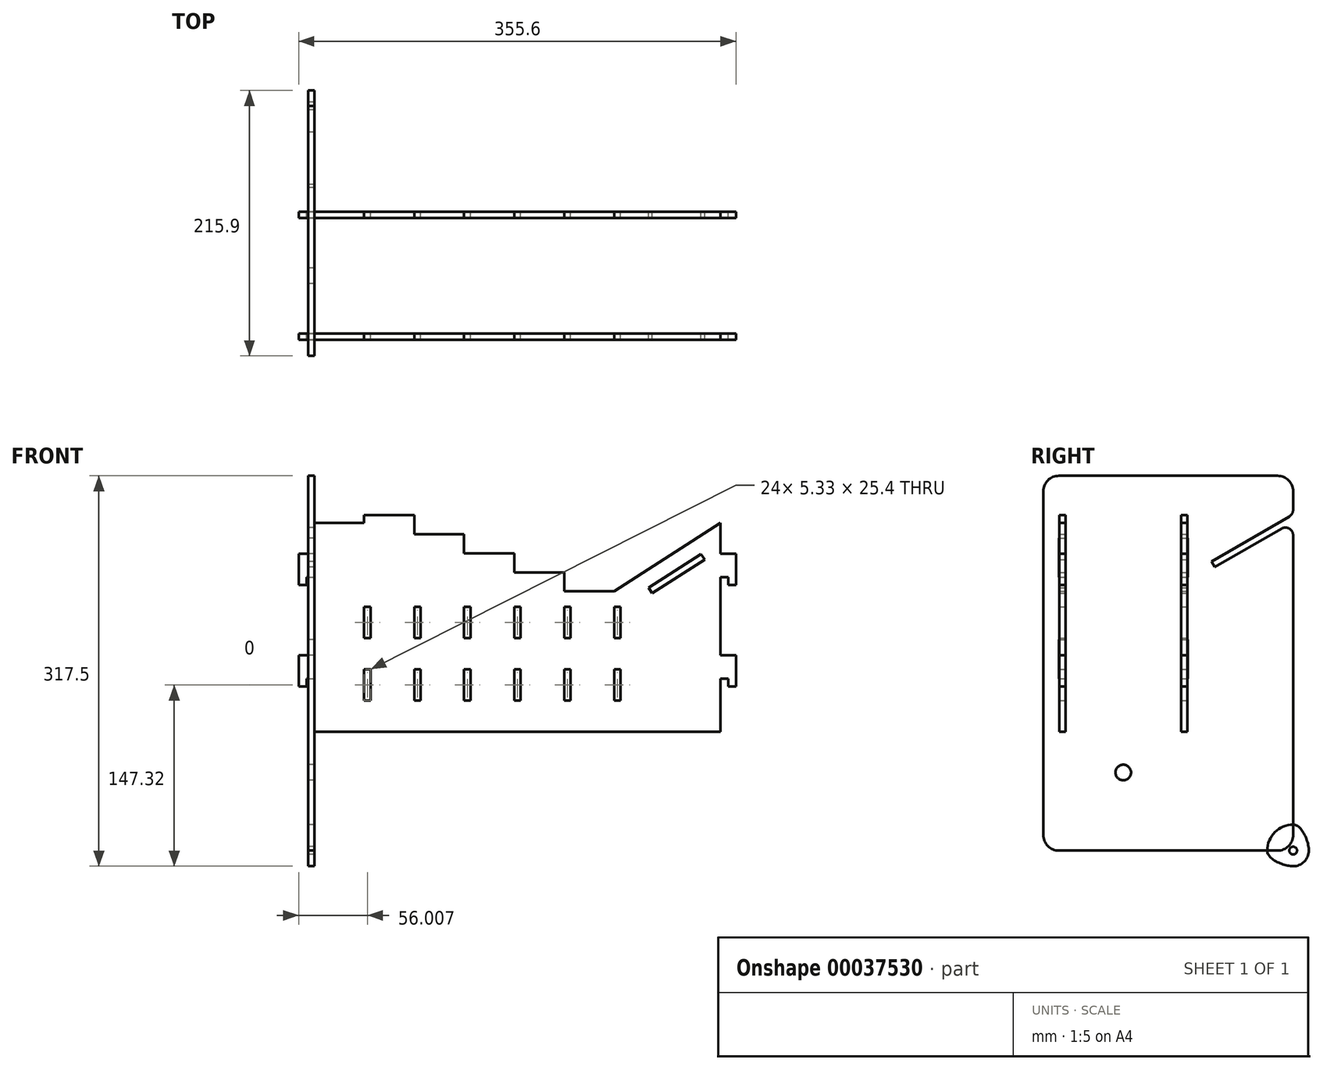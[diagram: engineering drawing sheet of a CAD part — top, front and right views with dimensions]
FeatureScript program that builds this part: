
annotation { "Feature Type Name" : "Feature", "Feature Type Description" : "" }
export const myFeature = defineFeature(function(context is Context, id is Id, definition is map)
    precondition{}
    {
        {
            var Q0;
            Q0=qCreatedBy(makeId("Right.planeOp"),FACE);
            var sketch = newSketch(context, id + "F0", { "sketchPlane" : qUnion([Q0])});
            skCircle(sketch, "E0", {"center": v(0, 0) * mm, "radius": 12.7 * mm});
            skArc(sketch, "E1", {"start": v(0, 21.08) * mm, "mid": v(-14.9, 14.9) * mm, "end": v(-21.08, 0) * mm});
            skLineSegment(sketch, "E2", {"start": v(0, 32.39) * mm, "end": v(0, -38.1) * mm, "construction": true});
            skLineSegment(sketch, "E3", {"start": v(-51.8, 0) * mm, "end": v(46.08, 0) * mm, "construction": true});
            skFitSpline(sketch, "E4", {"points": [v(0, 21.08) * mm, v(12.7, 0) * mm], "startDerivative": vector(20.97, 0) * mm, "endDerivative": vector(0, -23.76) * mm});
            skLineSegment(sketch, "E5", {"start": v(0, 0) * mm, "end": v(-27.33, 27.33) * mm, "construction": true});
            skFitSpline(sketch, "E6.MirrorCS", {"points": [v(-21.08, 0) * mm, v(0, -12.7) * mm], "startDerivative": vector(0, -20.97) * mm, "endDerivative": vector(23.76, 0) * mm});
            skCircle(sketch, "E7", {"center": v(0, 0) * mm, "radius": 3.18 * mm});
            skSolve(sketch);
        }
        {
            var Q0;
            Q0 = qSketchRegion(id + "F0", true);
            extrude(context, id + "F1", {"entities" : qUnion([Q0]), "depth" : 5.08 * mm});
        }
        {
            var Q0;
            Q0=qCreatedBy(makeId("Right.planeOp"),FACE);
            var sketch = newSketch(context, id + "F2", { "sketchPlane" : qUnion([Q0])});
            skLineSegment(sketch, "E8.bottom", {"start": v(-12.7, 0) * mm, "end": v(-190.5, 0) * mm});
            skLineSegment(sketch, "E8.top", {"start": v(-12.7, 304.8) * mm, "end": v(-190.5, 304.8) * mm});
            skLineSegment(sketch, "E8.left", {"start": v(0, 12.7) * mm, "end": v(0, 256.39) * mm});
            skLineSegment(sketch, "E8.right", {"start": v(-203.2, 12.7) * mm, "end": v(-203.2, 292.1) * mm});
            skLineSegment(sketch, "E9.bottom", {"start": v(-190.5, 254) * mm, "end": v(-185.17, 254) * mm});
            skLineSegment(sketch, "E9.top", {"start": v(-190.5, 139.7) * mm, "end": v(-185.17, 139.7) * mm});
            skLineSegment(sketch, "E9.left", {"start": v(-190.5, 254) * mm, "end": v(-190.5, 222.25) * mm});
            skLineSegment(sketch, "E9.right", {"start": v(-185.17, 254) * mm, "end": v(-185.17, 222.25) * mm});
            skLineSegment(sketch, "E10.bottom", {"start": v(-91.19, 254) * mm, "end": v(-85.85, 254) * mm});
            skLineSegment(sketch, "E10.top", {"start": v(-91.19, 139.7) * mm, "end": v(-85.85, 139.7) * mm});
            skLineSegment(sketch, "E10.left", {"start": v(-91.19, 254) * mm, "end": v(-91.19, 222.25) * mm});
            skLineSegment(sketch, "E10.right", {"start": v(-85.85, 254) * mm, "end": v(-85.85, 222.25) * mm});
            skLineSegment(sketch, "E11", {"start": v(-190.5, 222.25) * mm, "end": v(-185.17, 222.25) * mm});
            skLineSegment(sketch, "E12", {"start": v(-190.5, 171.45) * mm, "end": v(-185.17, 171.45) * mm});
            skLineSegment(sketch, "E13.trimOffspring", {"start": v(-91.19, 171.45) * mm, "end": v(-85.85, 171.45) * mm});
            skLineSegment(sketch, "E14.trimOffspring", {"start": v(-91.19, 222.25) * mm, "end": v(-85.85, 222.25) * mm});
            skLineSegment(sketch, "E15.trimOffspring", {"start": v(-185.17, 171.45) * mm, "end": v(-185.17, 139.7) * mm});
            skLineSegment(sketch, "E16.trimOffspring", {"start": v(-190.5, 171.45) * mm, "end": v(-190.5, 139.7) * mm});
            skLineSegment(sketch, "E17.trimOffspring", {"start": v(-85.85, 171.45) * mm, "end": v(-85.85, 139.7) * mm});
            skLineSegment(sketch, "E18.trimOffspring", {"start": v(-91.19, 171.45) * mm, "end": v(-91.19, 139.7) * mm});
            skLineSegment(sketch, "E19", {"start": v(-3.17, 271.71) * mm, "end": v(-66.37, 235.23) * mm});
            skLineSegment(sketch, "E20", {"start": v(-66.37, 235.23) * mm, "end": v(-63.7, 230.6) * mm});
            skLineSegment(sketch, "E21", {"start": v(-63.7, 230.6) * mm, "end": v(-9.53, 261.89) * mm});
            skLineSegment(sketch, "E22.trimOffspring", {"start": v(0, 277.21) * mm, "end": v(0, 292.1) * mm});
            skPoint(sketch, "E23.visualSharp", {"position": v(0, 304.8) * mm});
            skArc(sketch, "E23.filletArc", {"start": v(0, 292.1) * mm, "mid": v(-3.72, 301.08) * mm, "end": v(-12.7, 304.8) * mm});
            skPoint(sketch, "E24.visualSharp", {"position": v(-203.2, 304.8) * mm});
            skArc(sketch, "E24.filletArc", {"start": v(-190.5, 304.8) * mm, "mid": v(-199.48, 301.08) * mm, "end": v(-203.2, 292.1) * mm});
            skPoint(sketch, "E25.visualSharp", {"position": v(-203.2, 0) * mm});
            skArc(sketch, "E25.filletArc", {"start": v(-203.2, 12.7) * mm, "mid": v(-199.48, 3.72) * mm, "end": v(-190.5, 0) * mm});
            skPoint(sketch, "E26.visualSharp", {"position": v(0, 0) * mm});
            skArc(sketch, "E26.filletArc", {"start": v(-12.7, 0) * mm, "mid": v(-3.72, 3.72) * mm, "end": v(0, 12.7) * mm});
            skCircle(sketch, "E27", {"center": v(-138.18, 63.5) * mm, "radius": 6.35 * mm});
            skLineSegment(sketch, "E28", {"start": v(-185.17, 155.58) * mm, "end": v(-91.19, 155.58) * mm, "construction": true});
            skPoint(sketch, "E29", {"position": v(-138.18, 155.58) * mm});
            skPoint(sketch, "E30.visualSharp", {"position": v(0, 273.55) * mm});
            skArc(sketch, "E30.filletArc", {"start": v(-3.18, 271.71) * mm, "mid": v(-0.85, 274.04) * mm, "end": v(0, 277.21) * mm});
            skPoint(sketch, "E31.visualSharp", {"position": v(0, 267.39) * mm});
            skArc(sketch, "E31.filletArc", {"start": v(0, 256.39) * mm, "mid": v(-3.18, 261.89) * mm, "end": v(-9.53, 261.89) * mm});
            skSolve(sketch);
        }
        {
            var Q0;
            Q0=makeQuery(id+"F2.imprint","IMPRINT",FACE,{"disambiguationData":[TD([[makeQuery(id+"F2.imprint","IMPRINT",EDGE,{"derivedFrom":sQuery(id+"F2.wireOp",EDGE,"E8.bottom")}),-1.0]])]});
            extrude(context, id + "F3", {"entities" : qUnion([Q0]), "depth" : 5.08 * mm});
        }
        {
            var Q0;
            Q0=makeQuery(id+"F3.opExtrude","SWEPT_FACE",FACE,{"disambiguationData":[OSD([sQuery(id+"F2.wireOp",EDGE,"E9.right")])]});
            var sketch = newSketch(context, id + "F4", { "sketchPlane" : qUnion([Q0])});
            skLineSegment(sketch, "E32.0", {"start": v(0, 254) * mm, "end": v(0, 222.25) * mm});
            skLineSegment(sketch, "E32.1", {"start": v(0, 171.45) * mm, "end": v(0, 139.7) * mm});
            skLineSegment(sketch, "E33.0", {"start": v(5.08, 254) * mm, "end": v(5.08, 222.25) * mm});
            skLineSegment(sketch, "E33.1", {"start": v(5.08, 171.45) * mm, "end": v(5.08, 139.7) * mm});
            skLineSegment(sketch, "E34", {"start": v(5.08, 241.3) * mm, "end": v(-7.62, 241.3) * mm});
            skLineSegment(sketch, "E35", {"start": v(-7.62, 241.3) * mm, "end": v(-7.62, 215.9) * mm});
            skLineSegment(sketch, "E36", {"start": v(-7.62, 215.9) * mm, "end": v(-1.27, 215.9) * mm});
            skLineSegment(sketch, "E37", {"start": v(-1.27, 215.9) * mm, "end": v(-1.27, 222.25) * mm});
            skLineSegment(sketch, "E38", {"start": v(-1.27, 222.25) * mm, "end": v(5.08, 222.25) * mm});
            skLineSegment(sketch, "E39", {"start": v(5.08, 222.25) * mm, "end": v(5.08, 158.75) * mm});
            skLineSegment(sketch, "E40", {"start": v(5.08, 158.75) * mm, "end": v(-7.62, 158.75) * mm});
            skLineSegment(sketch, "E41", {"start": v(-7.62, 158.75) * mm, "end": v(-7.62, 133.35) * mm});
            skLineSegment(sketch, "E42", {"start": v(-7.62, 133.35) * mm, "end": v(-1.27, 133.35) * mm});
            skLineSegment(sketch, "E43", {"start": v(-1.27, 133.35) * mm, "end": v(-1.27, 139.7) * mm});
            skLineSegment(sketch, "E44", {"start": v(-1.27, 139.7) * mm, "end": v(5.08, 139.7) * mm});
            skLineSegment(sketch, "E45", {"start": v(5.08, 139.7) * mm, "end": v(5.08, 96.52) * mm});
            skLineSegment(sketch, "E46", {"start": v(5.08, 96.52) * mm, "end": v(335.28, 96.52) * mm});
            skLineSegment(sketch, "E47", {"start": v(5.08, 241.3) * mm, "end": v(5.08, 266.36) * mm});
            skLineSegment(sketch, "E48", {"start": v(5.08, 266.36) * mm, "end": v(45.72, 266.36) * mm});
            skLineSegment(sketch, "E49", {"start": v(45.72, 266.36) * mm, "end": v(45.72, 272.7) * mm});
            skLineSegment(sketch, "E50", {"start": v(45.72, 272.7) * mm, "end": v(86.36, 272.7) * mm});
            skLineSegment(sketch, "E51", {"start": v(170.18, 96.52) * mm, "end": v(170.18, 64.7) * mm, "construction": true});
            skLineSegment(sketch, "E52.MirrorCS", {"start": v(347.98, 241.3) * mm, "end": v(347.98, 215.9) * mm});
            skLineSegment(sketch, "E53.MirrorCS", {"start": v(335.28, 241.3) * mm, "end": v(347.98, 241.3) * mm});
            skLineSegment(sketch, "E54.MirrorCS", {"start": v(341.63, 222.25) * mm, "end": v(335.28, 222.25) * mm});
            skLineSegment(sketch, "E55.MirrorCS", {"start": v(341.63, 215.9) * mm, "end": v(341.63, 222.25) * mm});
            skLineSegment(sketch, "E56.MirrorCS", {"start": v(347.98, 215.9) * mm, "end": v(341.63, 215.9) * mm});
            skLineSegment(sketch, "E57.MirrorCS", {"start": v(335.28, 222.25) * mm, "end": v(335.28, 158.75) * mm});
            skLineSegment(sketch, "E58.MirrorCS", {"start": v(335.28, 158.75) * mm, "end": v(347.98, 158.75) * mm});
            skLineSegment(sketch, "E59.MirrorCS", {"start": v(347.98, 158.75) * mm, "end": v(347.98, 133.35) * mm});
            skLineSegment(sketch, "E60.MirrorCS", {"start": v(347.98, 133.35) * mm, "end": v(341.63, 133.35) * mm});
            skLineSegment(sketch, "E61.MirrorCS", {"start": v(341.63, 133.35) * mm, "end": v(341.63, 139.7) * mm});
            skLineSegment(sketch, "E62.MirrorCS", {"start": v(341.63, 139.7) * mm, "end": v(335.28, 139.7) * mm});
            skLineSegment(sketch, "E63.MirrorCS", {"start": v(335.28, 139.7) * mm, "end": v(335.28, 96.52) * mm});
            skLineSegment(sketch, "E64.bottom", {"start": v(45.72, 147.32) * mm, "end": v(51.05, 147.32) * mm});
            skLineSegment(sketch, "E64.top", {"start": v(45.72, 121.92) * mm, "end": v(51.05, 121.92) * mm});
            skLineSegment(sketch, "E64.left", {"start": v(45.72, 147.32) * mm, "end": v(45.72, 121.92) * mm});
            skLineSegment(sketch, "E64.right", {"start": v(51.05, 147.32) * mm, "end": v(51.05, 121.92) * mm});
            skLineSegment(sketch, "E65.bottom", {"start": v(45.72, 198.12) * mm, "end": v(51.05, 198.12) * mm});
            skLineSegment(sketch, "E65.top", {"start": v(45.72, 172.72) * mm, "end": v(51.05, 172.72) * mm});
            skLineSegment(sketch, "E65.left", {"start": v(45.72, 198.12) * mm, "end": v(45.72, 172.72) * mm});
            skLineSegment(sketch, "E65.right", {"start": v(51.05, 198.12) * mm, "end": v(51.05, 172.72) * mm});
            skLineSegment(sketch, "E66.1.0.0", {"start": v(86.36, 147.32) * mm, "end": v(86.36, 121.92) * mm});
            skLineSegment(sketch, "E66.1.0.1", {"start": v(86.36, 198.12) * mm, "end": v(86.36, 172.72) * mm});
            skLineSegment(sketch, "E66.1.0.2", {"start": v(86.36, 172.72) * mm, "end": v(91.7, 172.72) * mm});
            skLineSegment(sketch, "E66.1.0.3", {"start": v(91.7, 147.32) * mm, "end": v(91.7, 121.92) * mm});
            skLineSegment(sketch, "E66.1.0.4", {"start": v(86.36, 121.92) * mm, "end": v(91.7, 121.92) * mm});
            skLineSegment(sketch, "E66.1.0.5", {"start": v(86.36, 147.32) * mm, "end": v(91.7, 147.32) * mm});
            skLineSegment(sketch, "E66.1.0.6", {"start": v(86.36, 198.12) * mm, "end": v(91.7, 198.12) * mm});
            skLineSegment(sketch, "E66.1.0.7", {"start": v(91.7, 198.12) * mm, "end": v(91.7, 172.72) * mm});
            skLineSegment(sketch, "E66.2.0.0", {"start": v(127, 147.32) * mm, "end": v(127, 121.92) * mm});
            skLineSegment(sketch, "E66.2.0.1", {"start": v(127, 198.12) * mm, "end": v(127, 172.72) * mm});
            skLineSegment(sketch, "E66.2.0.2", {"start": v(127, 172.72) * mm, "end": v(132.33, 172.72) * mm});
            skLineSegment(sketch, "E66.2.0.3", {"start": v(132.33, 147.32) * mm, "end": v(132.33, 121.92) * mm});
            skLineSegment(sketch, "E66.2.0.4", {"start": v(127, 121.92) * mm, "end": v(132.33, 121.92) * mm});
            skLineSegment(sketch, "E66.2.0.5", {"start": v(127, 147.32) * mm, "end": v(132.33, 147.32) * mm});
            skLineSegment(sketch, "E66.2.0.6", {"start": v(127, 198.12) * mm, "end": v(132.33, 198.12) * mm});
            skLineSegment(sketch, "E66.2.0.7", {"start": v(132.33, 198.12) * mm, "end": v(132.33, 172.72) * mm});
            skLineSegment(sketch, "E66.3.0.0", {"start": v(167.64, 147.32) * mm, "end": v(167.64, 121.92) * mm});
            skLineSegment(sketch, "E66.3.0.1", {"start": v(167.64, 198.12) * mm, "end": v(167.64, 172.72) * mm});
            skLineSegment(sketch, "E66.3.0.2", {"start": v(167.64, 172.72) * mm, "end": v(172.97, 172.72) * mm});
            skLineSegment(sketch, "E66.3.0.3", {"start": v(172.97, 147.32) * mm, "end": v(172.97, 121.92) * mm});
            skLineSegment(sketch, "E66.3.0.4", {"start": v(167.64, 121.92) * mm, "end": v(172.97, 121.92) * mm});
            skLineSegment(sketch, "E66.3.0.5", {"start": v(167.64, 147.32) * mm, "end": v(172.97, 147.32) * mm});
            skLineSegment(sketch, "E66.3.0.6", {"start": v(167.64, 198.12) * mm, "end": v(172.97, 198.12) * mm});
            skLineSegment(sketch, "E66.3.0.7", {"start": v(172.97, 198.12) * mm, "end": v(172.97, 172.72) * mm});
            skLineSegment(sketch, "E66.4.0.0", {"start": v(208.28, 147.32) * mm, "end": v(208.28, 121.92) * mm});
            skLineSegment(sketch, "E66.4.0.1", {"start": v(208.28, 198.12) * mm, "end": v(208.28, 172.72) * mm});
            skLineSegment(sketch, "E66.4.0.2", {"start": v(208.28, 172.72) * mm, "end": v(213.61, 172.72) * mm});
            skLineSegment(sketch, "E66.4.0.3", {"start": v(213.61, 147.32) * mm, "end": v(213.61, 121.92) * mm});
            skLineSegment(sketch, "E66.4.0.4", {"start": v(208.28, 121.92) * mm, "end": v(213.61, 121.92) * mm});
            skLineSegment(sketch, "E66.4.0.5", {"start": v(208.28, 147.32) * mm, "end": v(213.61, 147.32) * mm});
            skLineSegment(sketch, "E66.4.0.6", {"start": v(208.28, 198.12) * mm, "end": v(213.61, 198.12) * mm});
            skLineSegment(sketch, "E66.4.0.7", {"start": v(213.61, 198.12) * mm, "end": v(213.61, 172.72) * mm});
            skLineSegment(sketch, "E66.5.0.0", {"start": v(248.92, 147.32) * mm, "end": v(248.92, 121.92) * mm});
            skLineSegment(sketch, "E66.5.0.1", {"start": v(248.92, 198.12) * mm, "end": v(248.92, 172.72) * mm});
            skLineSegment(sketch, "E66.5.0.2", {"start": v(248.92, 172.72) * mm, "end": v(254.25, 172.72) * mm});
            skLineSegment(sketch, "E66.5.0.3", {"start": v(254.25, 147.32) * mm, "end": v(254.25, 121.92) * mm});
            skLineSegment(sketch, "E66.5.0.4", {"start": v(248.92, 121.92) * mm, "end": v(254.25, 121.92) * mm});
            skLineSegment(sketch, "E66.5.0.5", {"start": v(248.92, 147.32) * mm, "end": v(254.25, 147.32) * mm});
            skLineSegment(sketch, "E66.5.0.6", {"start": v(248.92, 198.12) * mm, "end": v(254.25, 198.12) * mm});
            skLineSegment(sketch, "E66.5.0.7", {"start": v(254.25, 198.12) * mm, "end": v(254.25, 172.72) * mm});
            skLineSegment(sketch, "E66.direction1", {"start": v(45.72, 121.92) * mm, "end": v(86.36, 121.92) * mm, "construction": true});
            skLineSegment(sketch, "E67", {"start": v(86.36, 272.7) * mm, "end": v(86.36, 257.24) * mm});
            skLineSegment(sketch, "E68", {"start": v(86.36, 257.24) * mm, "end": v(127, 257.24) * mm});
            skLineSegment(sketch, "E69", {"start": v(127, 257.24) * mm, "end": v(127, 241.76) * mm});
            skLineSegment(sketch, "E70", {"start": v(127, 241.76) * mm, "end": v(167.64, 241.76) * mm});
            skLineSegment(sketch, "E71", {"start": v(167.64, 241.76) * mm, "end": v(167.64, 226.3) * mm});
            skLineSegment(sketch, "E72", {"start": v(167.64, 226.3) * mm, "end": v(208.28, 226.3) * mm});
            skLineSegment(sketch, "E73", {"start": v(208.28, 226.3) * mm, "end": v(208.28, 210.82) * mm});
            skLineSegment(sketch, "E74", {"start": v(208.28, 210.82) * mm, "end": v(248.92, 210.82) * mm});
            skLineSegment(sketch, "E75", {"start": v(248.92, 210.82) * mm, "end": v(335.28, 266.36) * mm});
            skLineSegment(sketch, "E76", {"start": v(335.28, 241.3) * mm, "end": v(335.28, 266.36) * mm});
            skLineSegment(sketch, "E77", {"start": v(276.97, 213.76) * mm, "end": v(319.7, 241.24) * mm});
            skLineSegment(sketch, "E78", {"start": v(319.7, 241.24) * mm, "end": v(322.58, 236.75) * mm});
            skLineSegment(sketch, "E79", {"start": v(322.58, 236.75) * mm, "end": v(279.85, 209.27) * mm});
            skLineSegment(sketch, "E80", {"start": v(279.85, 209.27) * mm, "end": v(276.97, 213.76) * mm});
            skSolve(sketch);
        }
        {
            var Q0;
            Q0 = qSketchRegion(id + "F4", true);
            extrude(context, id + "F5", {"entities" : qUnion([Q0]), "depth" : 5.08 * mm});
        }
        {
            var Q0;
            Q0=makeQuery(id+"F5.opExtrude","SWEPT_BODY",BODY,{"disambiguationData":[OSD([sQuery(id+"F4.wireOp",EDGE,"E34"),sQuery(id+"F4.wireOp",EDGE,"E35"),sQuery(id+"F4.wireOp",EDGE,"E36"),sQuery(id+"F4.wireOp",EDGE,"E37"),sQuery(id+"F4.wireOp",EDGE,"E38"),sQuery(id+"F4.wireOp",EDGE,"E39"),sQuery(id+"F4.wireOp",EDGE,"E40"),sQuery(id+"F4.wireOp",EDGE,"E41"),sQuery(id+"F4.wireOp",EDGE,"E42"),sQuery(id+"F4.wireOp",EDGE,"E43"),sQuery(id+"F4.wireOp",EDGE,"E44"),sQuery(id+"F4.wireOp",EDGE,"E45"),sQuery(id+"F4.wireOp",EDGE,"E46"),sQuery(id+"F4.wireOp",EDGE,"E47"),sQuery(id+"F4.wireOp",EDGE,"E48"),sQuery(id+"F4.wireOp",EDGE,"E49"),sQuery(id+"F4.wireOp",EDGE,"E50"),sQuery(id+"F4.wireOp",EDGE,"E52.MirrorCS"),sQuery(id+"F4.wireOp",EDGE,"E53.MirrorCS"),sQuery(id+"F4.wireOp",EDGE,"E54.MirrorCS"),sQuery(id+"F4.wireOp",EDGE,"E55.MirrorCS"),sQuery(id+"F4.wireOp",EDGE,"E56.MirrorCS"),sQuery(id+"F4.wireOp",EDGE,"E57.MirrorCS"),sQuery(id+"F4.wireOp",EDGE,"E58.MirrorCS"),sQuery(id+"F4.wireOp",EDGE,"E59.MirrorCS"),sQuery(id+"F4.wireOp",EDGE,"E60.MirrorCS"),sQuery(id+"F4.wireOp",EDGE,"E61.MirrorCS"),sQuery(id+"F4.wireOp",EDGE,"E62.MirrorCS"),sQuery(id+"F4.wireOp",EDGE,"E63.MirrorCS"),sQuery(id+"F4.wireOp",EDGE,"E64.bottom"),sQuery(id+"F4.wireOp",EDGE,"E64.top"),sQuery(id+"F4.wireOp",EDGE,"E64.left"),sQuery(id+"F4.wireOp",EDGE,"E64.right"),sQuery(id+"F4.wireOp",EDGE,"E65.bottom"),sQuery(id+"F4.wireOp",EDGE,"E65.top"),sQuery(id+"F4.wireOp",EDGE,"E65.left"),sQuery(id+"F4.wireOp",EDGE,"E65.right"),sQuery(id+"F4.wireOp",EDGE,"E66.1.0.0"),sQuery(id+"F4.wireOp",EDGE,"E66.1.0.1"),sQuery(id+"F4.wireOp",EDGE,"E66.1.0.2"),sQuery(id+"F4.wireOp",EDGE,"E66.1.0.3"),sQuery(id+"F4.wireOp",EDGE,"E66.1.0.4"),sQuery(id+"F4.wireOp",EDGE,"E66.1.0.5"),sQuery(id+"F4.wireOp",EDGE,"E66.1.0.6"),sQuery(id+"F4.wireOp",EDGE,"E66.1.0.7"),sQuery(id+"F4.wireOp",EDGE,"E66.2.0.0"),sQuery(id+"F4.wireOp",EDGE,"E66.2.0.1"),sQuery(id+"F4.wireOp",EDGE,"E66.2.0.2"),sQuery(id+"F4.wireOp",EDGE,"E66.2.0.3"),sQuery(id+"F4.wireOp",EDGE,"E66.2.0.4"),sQuery(id+"F4.wireOp",EDGE,"E66.2.0.5"),sQuery(id+"F4.wireOp",EDGE,"E66.2.0.6"),sQuery(id+"F4.wireOp",EDGE,"E66.2.0.7"),sQuery(id+"F4.wireOp",EDGE,"E66.3.0.0"),sQuery(id+"F4.wireOp",EDGE,"E66.3.0.1"),sQuery(id+"F4.wireOp",EDGE,"E66.3.0.2"),sQuery(id+"F4.wireOp",EDGE,"E66.3.0.3"),sQuery(id+"F4.wireOp",EDGE,"E66.3.0.4"),sQuery(id+"F4.wireOp",EDGE,"E66.3.0.5"),sQuery(id+"F4.wireOp",EDGE,"E66.3.0.6"),sQuery(id+"F4.wireOp",EDGE,"E66.3.0.7"),sQuery(id+"F4.wireOp",EDGE,"E66.4.0.0"),sQuery(id+"F4.wireOp",EDGE,"E66.4.0.1"),sQuery(id+"F4.wireOp",EDGE,"E66.4.0.2"),sQuery(id+"F4.wireOp",EDGE,"E66.4.0.3"),sQuery(id+"F4.wireOp",EDGE,"E66.4.0.4"),sQuery(id+"F4.wireOp",EDGE,"E66.4.0.5"),sQuery(id+"F4.wireOp",EDGE,"E66.4.0.6"),sQuery(id+"F4.wireOp",EDGE,"E66.4.0.7"),sQuery(id+"F4.wireOp",EDGE,"E66.5.0.0"),sQuery(id+"F4.wireOp",EDGE,"E66.5.0.1"),sQuery(id+"F4.wireOp",EDGE,"E66.5.0.2"),sQuery(id+"F4.wireOp",EDGE,"E66.5.0.3"),sQuery(id+"F4.wireOp",EDGE,"E66.5.0.4"),sQuery(id+"F4.wireOp",EDGE,"E66.5.0.5"),sQuery(id+"F4.wireOp",EDGE,"E66.5.0.6"),sQuery(id+"F4.wireOp",EDGE,"E66.5.0.7"),sQuery(id+"F4.wireOp",EDGE,"E67"),sQuery(id+"F4.wireOp",EDGE,"E68"),sQuery(id+"F4.wireOp",EDGE,"E69"),sQuery(id+"F4.wireOp",EDGE,"E70"),sQuery(id+"F4.wireOp",EDGE,"E71"),sQuery(id+"F4.wireOp",EDGE,"E72"),sQuery(id+"F4.wireOp",EDGE,"E73"),sQuery(id+"F4.wireOp",EDGE,"E74"),sQuery(id+"F4.wireOp",EDGE,"E75"),sQuery(id+"F4.wireOp",EDGE,"E76"),sQuery(id+"F4.wireOp",EDGE,"E77"),sQuery(id+"F4.wireOp",EDGE,"E78"),sQuery(id+"F4.wireOp",EDGE,"E79"),sQuery(id+"F4.wireOp",EDGE,"E80")])]});
            var Q1;
            Q1=sQuery(id+"F2.wireOp",EDGE,"E28");
            var Q2;
            Q2=sQuery(id+"F2.wireOp",EDGE,"E10.top");
            transform(context, id + "F6", {"entities" : qUnion([Q0]), "transformType" : TransformType.TRANSLATION_3D, "dx" : 0 * mm, "dy" : 99.06 * mm, "dz" : 0 * mm, "makeCopy" : true});
        }
    });
